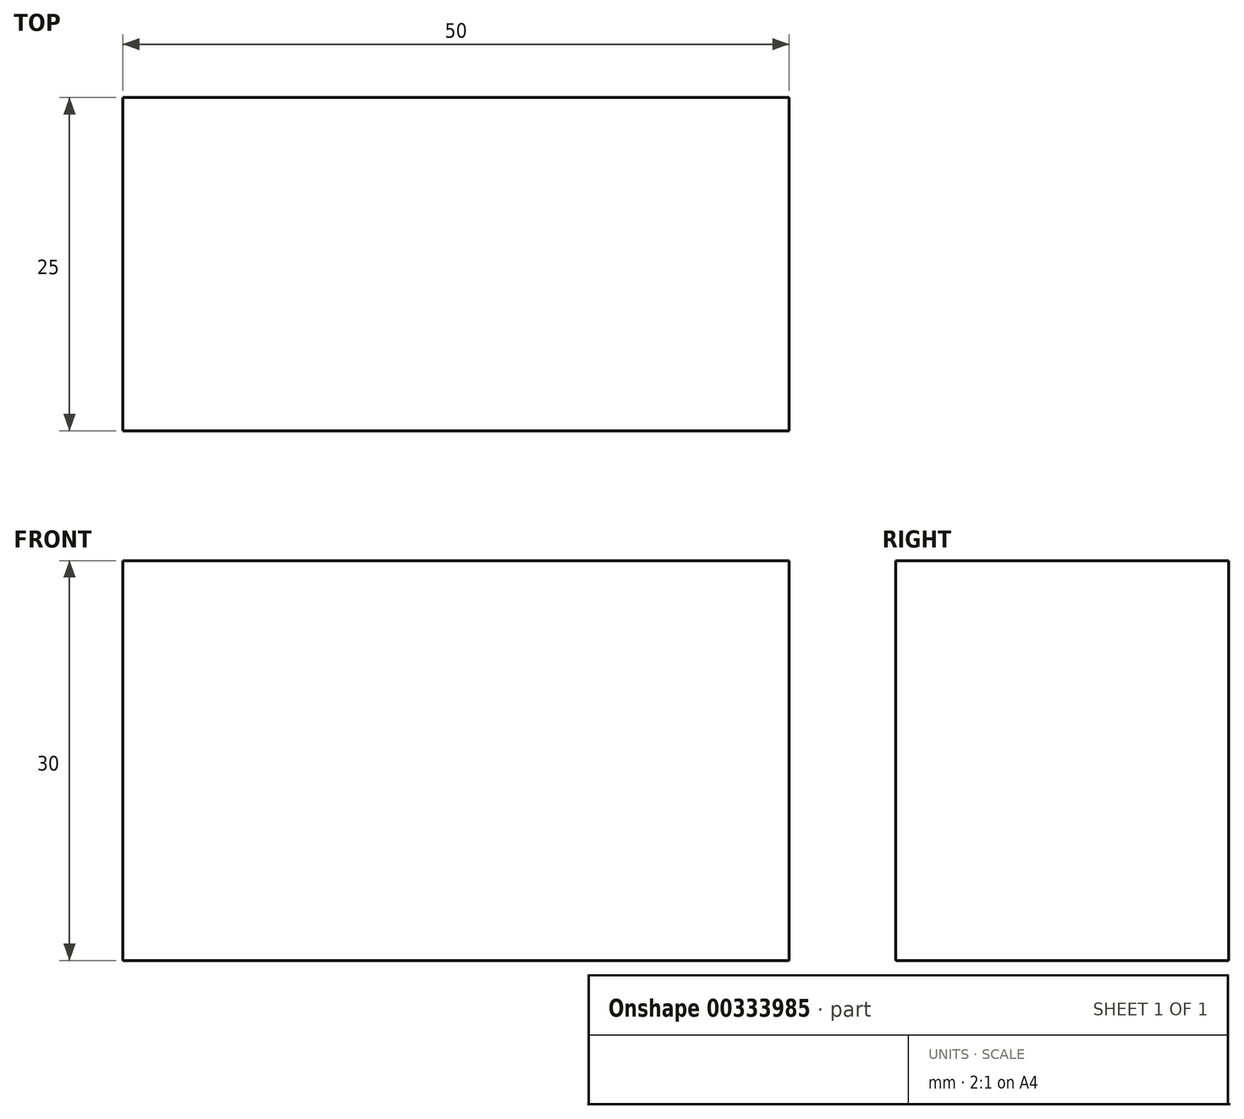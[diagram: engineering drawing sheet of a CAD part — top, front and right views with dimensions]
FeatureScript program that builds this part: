
annotation { "Feature Type Name" : "Feature", "Feature Type Description" : "" }
export const myFeature = defineFeature(function(context is Context, id is Id, definition is map)
    precondition{}
    {
        {
            var Q0;
            Q0=qCreatedBy(makeId("Front.planeOp"),FACE);
            var sketch = newSketch(context, id + "F0", { "sketchPlane" : qUnion([Q0])});
            skLineSegment(sketch, "E0.bottom", {"start": v(-50.97, 5.57) * mm, "end": v(-0.97, 5.57) * mm});
            skLineSegment(sketch, "E0.top", {"start": v(-50.97, -24.43) * mm, "end": v(-0.97, -24.43) * mm});
            skLineSegment(sketch, "E0.left", {"start": v(-50.97, 5.57) * mm, "end": v(-50.97, -24.43) * mm});
            skLineSegment(sketch, "E0.right", {"start": v(-0.97, 5.57) * mm, "end": v(-0.97, -24.43) * mm});
            skSolve(sketch);
        }
        {
            var Q0;
            Q0 = qSketchRegion(id + "F0", true);
            extrude(context, id + "F1", {"entities" : qUnion([Q0]), "depth" : 25 * mm});
        }
    });
